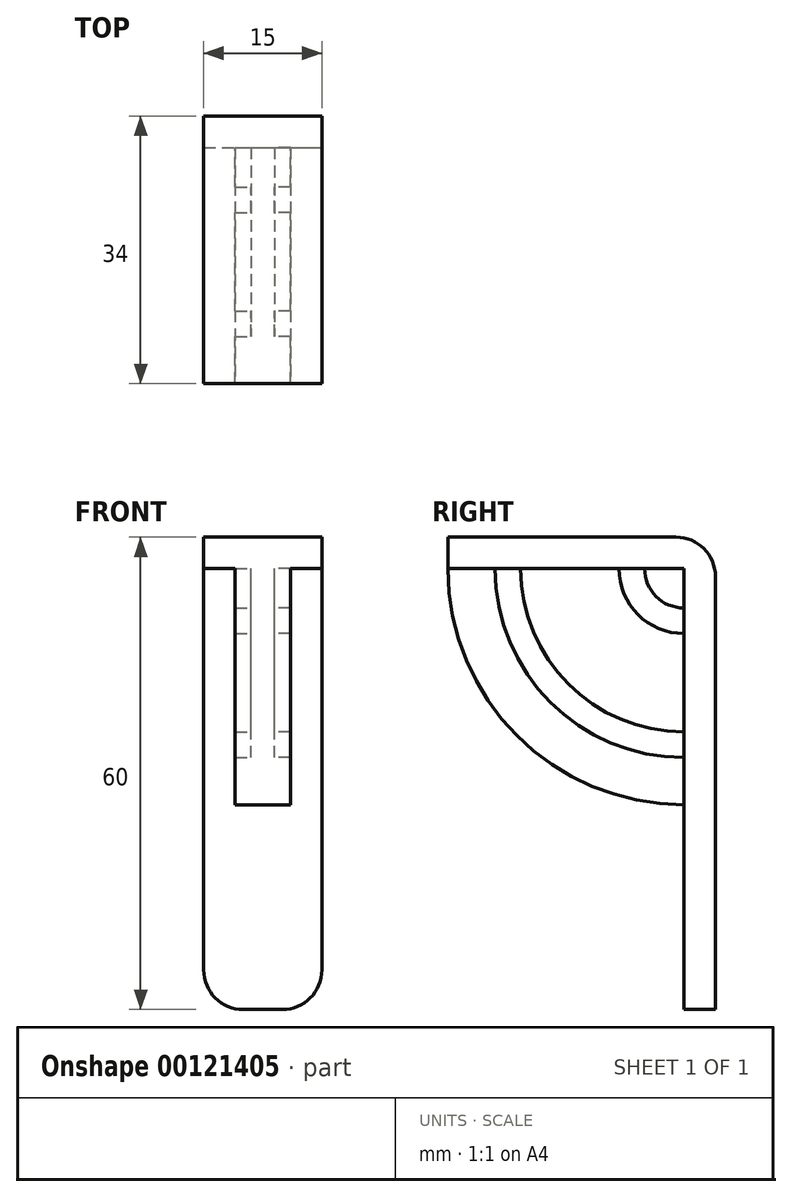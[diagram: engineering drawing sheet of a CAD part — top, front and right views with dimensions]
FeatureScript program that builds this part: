
annotation { "Feature Type Name" : "Feature", "Feature Type Description" : "" }
export const myFeature = defineFeature(function(context is Context, id is Id, definition is map)
    precondition{}
    {
        {
            var Q0;
            Q0=qCreatedBy(makeId("Front.planeOp"),FACE);
            var sketch = newSketch(context, id + "F0", { "sketchPlane" : qUnion([Q0])});
            skLineSegment(sketch, "E0.bottom", {"start": v(-4.93, 31) * mm, "end": v(10.07, 31) * mm});
            skLineSegment(sketch, "E0.top", {"start": v(-4.93, -29) * mm, "end": v(10.07, -29) * mm});
            skLineSegment(sketch, "E0.left", {"start": v(-4.93, 31) * mm, "end": v(-4.93, -29) * mm});
            skLineSegment(sketch, "E0.right", {"start": v(10.07, 31) * mm, "end": v(10.07, -29) * mm});
            skSolve(sketch);
        }
        {
            var Q0;
            Q0=makeQuery(id+"F0.imprint","IMPRINT",FACE,{"disambiguationData":[TD([[makeQuery(id+"F0.imprint","IMPRINT",EDGE,{"derivedFrom":sQuery(id+"F0.wireOp",EDGE,"E0.bottom")}),-1.0]])]});
            extrude(context, id + "F1", {"entities" : qUnion([Q0]), "depth" : 4 * mm});
        }
        {
            var Q0;
            Q0=makeQuery(id+"F1.opExtrude","CAP_FACE",FACE,{"disambiguationData":[OSD([sQuery(id+"F0.wireOp",EDGE,"E0.bottom"),sQuery(id+"F0.wireOp",EDGE,"E0.top"),sQuery(id+"F0.wireOp",EDGE,"E0.left"),sQuery(id+"F0.wireOp",EDGE,"E0.right")])],"isStart":false});
            var sketch = newSketch(context, id + "F2", { "sketchPlane" : qUnion([Q0])});
            skLineSegment(sketch, "E1.bottom", {"start": v(-4.93, 31) * mm, "end": v(10.07, 31) * mm});
            skLineSegment(sketch, "E1.top", {"start": v(-4.93, 27) * mm, "end": v(10.07, 27) * mm});
            skLineSegment(sketch, "E1.left", {"start": v(-4.93, 31) * mm, "end": v(-4.93, 27) * mm});
            skLineSegment(sketch, "E1.right", {"start": v(10.07, 31) * mm, "end": v(10.07, 27) * mm});
            skSolve(sketch);
        }
        {
            var Q0;
            Q0=makeQuery(id+"F2.imprint","IMPRINT",FACE,{"disambiguationData":[TD([[makeQuery(id+"F2.imprint","IMPRINT",EDGE,{"derivedFrom":sQuery(id+"F2.wireOp",EDGE,"E1.bottom")}),-1.0]])]});
            extrude(context, id + "F3", {"entities" : qUnion([Q0]), "operationType" : NewBodyOperationType.ADD, "depth" : 30 * mm});
        }
        {
            var Q0;
            Q0=makeQuery(id+"F3.opExtrude","SWEPT_FACE",FACE,{"disambiguationData":[OSD([sQuery(id+"F2.wireOp",EDGE,"E1.top")])]});
            var sketch = newSketch(context, id + "F4", { "sketchPlane" : qUnion([Q0])});
            skLineSegment(sketch, "E2.bottom", {"start": v(6.07, 34) * mm, "end": v(-0.93, 34) * mm});
            skLineSegment(sketch, "E2.top", {"start": v(6.07, 4) * mm, "end": v(-0.93, 4) * mm});
            skLineSegment(sketch, "E2.left", {"start": v(6.07, 34) * mm, "end": v(6.07, 4) * mm});
            skLineSegment(sketch, "E2.right", {"start": v(-0.93, 34) * mm, "end": v(-0.93, 4) * mm});
            skLineSegment(sketch, "E3.bottom", {"start": v(-0.93, 12.25) * mm, "end": v(1.07, 12.25) * mm});
            skLineSegment(sketch, "E3.top", {"start": v(-0.93, 9) * mm, "end": v(1.07, 9) * mm});
            skLineSegment(sketch, "E3.left", {"start": v(-0.93, 12.25) * mm, "end": v(-0.93, 9) * mm});
            skLineSegment(sketch, "E3.right", {"start": v(1.07, 12.25) * mm, "end": v(1.07, 9) * mm});
            skLineSegment(sketch, "E4.bottom", {"start": v(6.07, 12.25) * mm, "end": v(4.07, 12.25) * mm});
            skLineSegment(sketch, "E4.top", {"start": v(6.07, 9) * mm, "end": v(4.07, 9) * mm});
            skLineSegment(sketch, "E4.left", {"start": v(6.07, 12.25) * mm, "end": v(6.07, 9) * mm});
            skLineSegment(sketch, "E4.right", {"start": v(4.07, 12.25) * mm, "end": v(4.07, 9) * mm});
            skLineSegment(sketch, "E5.bottom", {"start": v(-0.93, 28) * mm, "end": v(1.07, 28) * mm});
            skLineSegment(sketch, "E5.top", {"start": v(-0.93, 24.75) * mm, "end": v(1.07, 24.75) * mm});
            skLineSegment(sketch, "E5.left", {"start": v(-0.93, 28) * mm, "end": v(-0.93, 24.75) * mm});
            skLineSegment(sketch, "E5.right", {"start": v(1.07, 28) * mm, "end": v(1.07, 24.75) * mm});
            skPoint(sketch, "E6.firstSnap0", {"position": v(0.07, 28) * mm});
            skLineSegment(sketch, "E6.bottom", {"start": v(6.07, 28) * mm, "end": v(4.07, 28) * mm});
            skLineSegment(sketch, "E6.top", {"start": v(6.07, 24.75) * mm, "end": v(4.07, 24.75) * mm});
            skLineSegment(sketch, "E6.left", {"start": v(6.07, 28) * mm, "end": v(6.07, 24.75) * mm});
            skLineSegment(sketch, "E6.right", {"start": v(4.07, 28) * mm, "end": v(4.07, 24.75) * mm});
            skSolve(sketch);
        }
        {
            var Q0;
            {var subQ7=sQuery(id+"F4.wireOp",EDGE,"E2.bottom");Q0=makeQuery(id+"F4.imprint","IMPRINT",FACE,{"disambiguationData":[TD([[makeQuery(id+"F4.imprint","IMPRINT",EDGE,{"derivedFrom":subQ7}),-1.0]])]});}
            var Q1;
            Q1=sQuery(id+"F4.wireOp",EDGE,"E2.top");
            revolve(context, id + "F5", {"operationType" : NewBodyOperationType.ADD, "entities" : qUnion([Q0]), "axis" : qUnion([Q1]), "revolveType" : RevolveType.ONE_DIRECTION, "oppositeDirection" : true, "angle" : 90 * degree});
        }
        {
            var Q0;
            {var subQ0=sQuery(id+"F4.wireOp",EDGE,"E2.right");Q0=makeQuery(id+"F5.opRevolve","SWEPT_FACE",FACE,{"disambiguationData":[OSD([subQ0]),TDD([makeQuery(id+"F4.imprint","IMPRINT",EDGE,{"disambiguationData":[TD([[makeQuery(id+"F4.imprint","INTERSECT",VERTEX,{"derivedFrom":[makeQuery(id+"F3.opExtrude","CAP_EDGE",EDGE,{"disambiguationData":[OSD([sQuery(id+"F2.wireOp",EDGE,"E1.top")])],"isStart":false}),sQuery(id+"F4.wireOp",EDGE,"E2.bottom"),subQ0]}),-1.0]])],"derivedFrom":subQ0})])]});}
            var sketch = newSketch(context, id + "F6", { "sketchPlane" : qUnion([Q0])});
            skLineSegment(sketch, "E7.bottom", {"start": v(8.9, 27) * mm, "end": v(12.16, 27) * mm});
            skLineSegment(sketch, "E7.top", {"start": v(8.9, -4.98) * mm, "end": v(12.16, -4.98) * mm});
            skLineSegment(sketch, "E7.left", {"start": v(8.9, 27) * mm, "end": v(8.9, -4.98) * mm});
            skLineSegment(sketch, "E7.right", {"start": v(12.16, 27) * mm, "end": v(12.16, -4.98) * mm});
            skLineSegment(sketch, "E8.bottom", {"start": v(24.68, 26.95) * mm, "end": v(27.93, 26.95) * mm});
            skLineSegment(sketch, "E8.top", {"start": v(24.68, 3.01) * mm, "end": v(27.93, 3.01) * mm});
            skLineSegment(sketch, "E8.left", {"start": v(24.68, 26.95) * mm, "end": v(24.68, 3.01) * mm});
            skLineSegment(sketch, "E8.right", {"start": v(27.93, 26.95) * mm, "end": v(27.93, 3.01) * mm});
            skSolve(sketch);
        }
        {
            var Q0;
            {var subQ0=sQuery(id+"F4.wireOp",EDGE,"E2.left");Q0=makeQuery(id+"F5.opRevolve","SWEPT_FACE",FACE,{"disambiguationData":[OSD([subQ0]),TDD([makeQuery(id+"F4.imprint","IMPRINT",EDGE,{"disambiguationData":[TD([[makeQuery(id+"F4.imprint","INTERSECT",VERTEX,{"derivedFrom":[makeQuery(id+"F3.opExtrude","CAP_EDGE",EDGE,{"disambiguationData":[OSD([sQuery(id+"F2.wireOp",EDGE,"E1.top")])],"isStart":false}),sQuery(id+"F4.wireOp",EDGE,"E2.bottom"),subQ0]}),-1.0]])],"derivedFrom":subQ0})])]});}
            var sketch = newSketch(context, id + "F7", { "sketchPlane" : qUnion([Q0])});
            skLineSegment(sketch, "E9.bottom", {"start": v(-28, 27) * mm, "end": v(-24.75, 27) * mm});
            skLineSegment(sketch, "E9.top", {"start": v(-28, -1.66) * mm, "end": v(-24.75, -1.66) * mm});
            skLineSegment(sketch, "E9.left", {"start": v(-28, 27) * mm, "end": v(-28, -1.66) * mm});
            skLineSegment(sketch, "E9.right", {"start": v(-24.75, 27) * mm, "end": v(-24.75, -1.66) * mm});
            skLineSegment(sketch, "E10.bottom", {"start": v(-12.08, 26.94) * mm, "end": v(-8.83, 26.94) * mm});
            skLineSegment(sketch, "E10.top", {"start": v(-12.08, -7.13) * mm, "end": v(-8.83, -7.13) * mm});
            skLineSegment(sketch, "E10.left", {"start": v(-12.08, 26.94) * mm, "end": v(-12.08, -7.13) * mm});
            skLineSegment(sketch, "E10.right", {"start": v(-8.83, 26.94) * mm, "end": v(-8.83, -7.13) * mm});
            skSolve(sketch);
        }
        {
            var Q0;
            Q0=makeQuery(id+"F1.opExtrude","CAP_EDGE",EDGE,{"disambiguationData":[OSD([sQuery(id+"F0.wireOp",EDGE,"E0.bottom")])],"isStart":true});
            fillet(context, id + "F8", {"entities" : qUnion([Q0]), "radius" : 5 * mm, "tangentPropagation" : true, "allowEdgeOverflow" : false});
        }
        {
            var Q0;
            Q0=makeQuery(id+"F1.opExtrude","SWEPT_EDGE",EDGE,{"disambiguationData":[OSD([sQuery(id+"F0.wireOp",EDGE,"E0.top"),sQuery(id+"F0.wireOp",EDGE,"E0.right")])]});
            var Q1;
            Q1=makeQuery(id+"F1.opExtrude","SWEPT_EDGE",EDGE,{"disambiguationData":[OSD([sQuery(id+"F0.wireOp",EDGE,"E0.top"),sQuery(id+"F0.wireOp",EDGE,"E0.left")])]});
            fillet(context, id + "F9", {"entities" : qUnion([Q0, Q1]), "radius" : 5 * mm, "tangentPropagation" : true, "allowEdgeOverflow" : false});
        }
    });
